# Revit family: ВПВО
name_source: partatom
category: Оборудование
units: mm (PartAtom-declared; Revit-internal decimal feet)

## family parameters
Всегда вертикально = Да
Классификация = Нет
На основе рабочей плоскости = Нет
Общий = Нет
При загрузке вырезать с полостями = Нет
Размер круглого соединителя = Использовать диаметр
Тип детали = Нормальный
Точка принадлежности помещению = Нет

## types (159) — shared parameters
00_20_Name = Осьовий вентилятор середнього тиску
Casing Material = Условный материал-отделка
Grid Material = Условный материал-отделка
Load Classification = HVAC
Maintenance zone material = <По категории>
Number of Fase = 3
Voltage = 400 В
t = 5 мм
zero-valued in all types: Отметка по умолчанию

## per-type parameters (varying)
| type | D2 | D3 | Dn | Dy | L | Lk1 | Lk2 | Lk3 | Ly | Maximum Air Flow | Power | Rk | Rk1 | t1 | Вес |
| ВПВО-400-2Д/0,55-6/25/ПАГ | 490 мм | 390 мм | 404 мм | 400 мм | 350 мм | 170 мм | 300 мм | 235 мм | 175 мм | 1450.0 л/с | 550 В·А | 200 мм | 215 мм | 345 мм | 23.4 кг |
| ВПВО-400-2Д/0,75-6/30/ПАГ | 490 мм | 390 мм | 404 мм | 400 мм | 350 мм | 170 мм | 300 мм | 235 мм | 175 мм | 1700.0 л/с | 750 В·А | 200 мм | 215 мм | 345 мм | 26.5 кг |
| ВПВО-400-2Д/1,1-6/35/ПАГ | 490 мм | 390 мм | 404 мм | 400 мм | 450 мм | 270 мм | 400 мм | 335 мм | 225 мм | 2000.0 л/с | 1100 В·А | 200 мм | 215 мм | 445 мм | 27 кг |
| ВПВО-400-2Д/1,5-6/40/ПАГ | 490 мм | 390 мм | 404 мм | 400 мм | 450 мм | 270 мм | 400 мм | 335 мм | 225 мм | 2150.0 л/с | 1500 В·А | 200 мм | 215 мм | 445 мм | 32.5 кг |
| ВПВО-400-2Д/2,2-6/45/ПАГ | 490 мм | 390 мм | 404 мм | 400 мм | 450 мм | 270 мм | 400 мм | 335 мм | 225 мм | 2350.0 л/с | 2200 В·А | 200 мм | 215 мм | 445 мм | 34.5 кг |
| ВПВО-400-2Д/2,2-8/45/ПАГ | 490 мм | 390 мм | 404 мм | 400 мм | 450 мм | 270 мм | 400 мм | 335 мм | 225 мм | 2450.0 л/с | 2200 В·А | 200 мм | 215 мм | 445 мм | 35 кг |
| ВПВО-400-4Д/0,12-6/30/ПАГ | 490 мм | 390 мм | 404 мм | 400 мм | 350 мм | 170 мм | 300 мм | 235 мм | 175 мм | 880.0 л/с | 120 В·А | 200 мм | 215 мм | 345 мм | 19.5 кг |
| ВПВО-400-4Д/0,18-6/35/ПАГ | 490 мм | 390 мм | 404 мм | 400 мм | 350 мм | 170 мм | 300 мм | 235 мм | 175 мм | 1000.0 л/с | 180 В·А | 200 мм | 215 мм | 345 мм | 19.8 кг |
| ВПВО-400-4Д/0,18-6/40/ПАГ | 490 мм | 390 мм | 404 мм | 400 мм | 350 мм | 170 мм | 300 мм | 235 мм | 175 мм | 1050.0 л/с | 180 В·А | 200 мм | 215 мм | 345 мм | 19.8 кг |
| ВПВО-400-4Д/0,25-6/45/ПАГ | 490 мм | 390 мм | 404 мм | 400 мм | 350 мм | 170 мм | 300 мм | 235 мм | 175 мм | 1180.0 л/с | 250 В·А | 200 мм | 215 мм | 345 мм | 23.2 кг |
| ВПВО-400-4Д/0,37-8/45/ПАГ | 490 мм | 390 мм | 404 мм | 400 мм | 350 мм | 170 мм | 300 мм | 235 мм | 175 мм | 1200.0 л/с | 370 В·А | 200 мм | 215 мм | 345 мм | 23.9 кг |
| ВПВО-450-2Д/0,75-6/25/ПАГ | 540 мм | 440 мм | 454 мм | 450 мм | 350 мм | 170 мм | 300 мм | 235 мм | 175 мм | 1875.0 л/с | 750 В·А | 225 мм | 240 мм | 345 мм | 36.1 кг |
| ВПВО-450-2Д/1,1-6/30/ПАГ | 540 мм | 440 мм | 454 мм | 450 мм | 450 мм | 270 мм | 400 мм | 335 мм | 225 мм | 2300.0 л/с | 1100 В·А | 225 мм | 240 мм | 445 мм | 36.6 кг |
| ВПВО-450-2Д/1,5-6/35/ПАГ | 540 мм | 440 мм | 454 мм | 450 мм | 450 мм | 270 мм | 400 мм | 335 мм | 225 мм | 2700.0 л/с | 1500 В·А | 225 мм | 240 мм | 445 мм | 42.1 кг |
| ВПВО-450-2Д/2,2-6/40/ПАГ | 540 мм | 440 мм | 454 мм | 450 мм | 450 мм | 270 мм | 400 мм | 335 мм | 225 мм | 3000.0 л/с | 2200 В·А | 225 мм | 240 мм | 445 мм | 44.1 кг |
| ВПВО-450-2Д/3-8/40/ПАГ | 540 мм | 440 мм | 454 мм | 450 мм | 450 мм | 270 мм | 400 мм | 335 мм | 225 мм | 3125.0 л/с | 3000 В·А | 225 мм | 240 мм | 445 мм | 53.6 кг |
| ВПВО-450-2Д/4-8/45/ПАГ | 540 мм | 440 мм | 454 мм | 450 мм | 550 мм | 370 мм | 500 мм | 435 мм | 275 мм | 3500.0 л/с | 4000 В·А | 225 мм | 240 мм | 545 мм | 63.7 кг |
| ВПВО-450-4Д/0,12-6/25/ПАГ | 540 мм | 440 мм | 454 мм | 450 мм | 350 мм | 170 мм | 300 мм | 235 мм | 175 мм | 950.0 л/с | 120 В·А | 225 мм | 240 мм | 345 мм | 29.1 кг |
| ВПВО-450-4Д/0,18-6/30/ПАГ | 540 мм | 440 мм | 454 мм | 450 мм | 350 мм | 170 мм | 300 мм | 235 мм | 175 мм | 1100.0 л/с | 180 В·А | 225 мм | 240 мм | 345 мм | 29.4 кг |
| ВПВО-450-4Д/0,25-6/35/ПАГ | 540 мм | 440 мм | 454 мм | 450 мм | 350 мм | 170 мм | 300 мм | 235 мм | 175 мм | 1350.0 л/с | 250 В·А | 225 мм | 240 мм | 345 мм | 32.8 кг |
| ВПВО-450-4Д/0,25-6/40/ПАГ | 540 мм | 440 мм | 454 мм | 450 мм | 350 мм | 170 мм | 300 мм | 235 мм | 175 мм | 1450.0 л/с | 250 В·А | 225 мм | 240 мм | 345 мм | 32.8 кг |
| ВПВО-450-4Д/0,37-6/45/ПАГ | 540 мм | 440 мм | 454 мм | 450 мм | 350 мм | 170 мм | 300 мм | 235 мм | 175 мм | 1600.0 л/с | 370 В·А | 225 мм | 240 мм | 345 мм | 33 кг |
| ВПВО-450-4Д/0,55-8/45/ПАГ | 540 мм | 440 мм | 454 мм | 450 мм | 350 мм | 170 мм | 300 мм | 235 мм | 175 мм | 1700.0 л/с | 550 В·А | 225 мм | 240 мм | 345 мм | 36.6 кг |
| ВПВО-500-2Д/1,1-6/25/ПАГ | 600 мм | 490 мм | 504 мм | 500 мм | 450 мм | 270 мм | 400 мм | 335 мм | 225 мм | 2350.0 л/с | 1100 В·А | 250 мм | 265 мм | 445 мм | 48.2 кг |
| ВПВО-560-2Д/1,5-6/25/ПАГ | 660 мм | 550 мм | 564 мм | 560 мм | 450 мм | 270 мм | 400 мм | 335 мм | 225 мм | 2900.0 л/с | 1500 В·А | 280 мм | 295 мм | 445 мм | 70.8 кг |
| ВПВО-630-2Д/3-8/25/ПАГ | 730 мм | 620 мм | 634 мм | 630 мм | 450 мм | 270 мм | 400 мм | 335 мм | 225 мм | 3800.0 л/с | 3000 В·А | 315 мм | 330 мм | 445 мм | 88 кг |
| ВПВО-710-2Д/7,5-6/20/ПАГ | 810 мм | 700 мм | 714 мм | 710 мм | 550 мм | 370 мм | 500 мм | 435 мм | 275 мм | 6300.0 л/с | 7500 В·А | 355 мм | 370 мм | 545 мм | 150.8 |
| ВПВО-800-4Д/1,1-6/20/ПАГ | 900 мм | 790 мм | 804 мм | 800 мм | 450 мм | 270 мм | 400 мм | 335 мм | 225 мм | 4200.0 л/с | 1100 В·А | 400 мм | 415 мм | 445 мм | 115.6 кг |
| ВПВО-900-4Д/3-8/20/ПАГ | 1015 мм | 890 мм | 904 мм | 900 мм | 550 мм | 370 мм | 500 мм | 435 мм | 275 мм | 6000.0 л/с | 3000 В·А | 450 мм | 465 мм | 545 мм | 134.8 кг |
| ВПВО-1000-4Д/5,5-8/25/ПАГ | 1115 мм | 990 мм | 1004 мм | 1000 мм | 550 мм | 370 мм | 500 мм | 435 мм | 275 мм | 8600.0 л/с | 5500 В·А | 500 мм | 515 мм | 545 мм | 200.5 кг |
| ВПВО-1120-4Д/7,5-8/25/ПАГ | 1270 мм | 1110 мм | 1124 мм | 1120 мм | 650 мм | 470 мм | 600 мм | 535 мм | 325 мм | 12200.0 л/с | 7500 В·А | 560 мм | 575 мм | 645 мм | 222 кг |
| ВПВО-1250-4Д/7,5-8/25/ПАГ | 1400 мм | 1240 мм | 1254 мм | 1250 мм | 650 мм | 470 мм | 600 мм | 535 мм | 325 мм | 12500.0 л/с | 7500 В·А | 625 мм | 640 мм | 645 мм | 241 кг |
| ВПВО-500-2Д/1,5-6/30/ПАГ | 600 мм | 490 мм | 504 мм | 500 мм | 450 мм | 270 мм | 400 мм | 335 мм | 225 мм | 2900.0 л/с | 1500 В·А | 250 мм | 265 мм | 445 мм | 53.7 кг |
| ВПВО-500-2Д/2,2-6/35/ПАГ | 600 мм | 490 мм | 504 мм | 500 мм | 450 мм | 270 мм | 400 мм | 335 мм | 225 мм | 3400.0 л/с | 2200 В·А | 250 мм | 265 мм | 445 мм | 55.7 кг |
| ВПВО-500-2Д/3-8/35/ПАГ | 600 мм | 490 мм | 504 мм | 500 мм | 450 мм | 270 мм | 400 мм | 335 мм | 225 мм | 3700.0 л/с | 3000 В·А | 250 мм | 265 мм | 445 мм | 65.3 кг |
| ВПВО-500-2Д/4-8/40/ПАГ | 600 мм | 490 мм | 504 мм | 500 мм | 550 мм | 370 мм | 500 мм | 435 мм | 275 мм | 4200.0 л/с | 4000 В·А | 250 мм | 265 мм | 545 мм | 75.4 кг |
| ВПВО-500-2Д/5,5-8/45/ПАГ | 600 мм | 490 мм | 504 мм | 500 мм | 550 мм | 370 мм | 500 мм | 435 мм | 275 мм | 4500.0 л/с | 5500 В·А | 250 мм | 265 мм | 545 мм | 96.8 кг |
| ВПВО-500-4Д/0,18-6/25/ПАГ | 600 мм | 490 мм | 504 мм | 500 мм | 350 мм | 170 мм | 300 мм | 235 мм | 175 мм | 1200.0 л/с | 180 В·А | 250 мм | 265 мм | 345 мм | 61.5 кг |
| ВПВО-500-4Д/0,25-6/30/ПАГ | 600 мм | 490 мм | 504 мм | 500 мм | 350 мм | 170 мм | 300 мм | 235 мм | 175 мм | 1460.0 л/с | 250 В·А | 250 мм | 265 мм | 345 мм | 61.7 кг |
| ВПВО-500-4Д/0,37-6/35/ПАГ | 600 мм | 490 мм | 504 мм | 500 мм | 350 мм | 170 мм | 300 мм | 235 мм | 175 мм | 1700.0 л/с | 370 В·А | 250 мм | 265 мм | 345 мм | 64.8 кг |
| ВПВО-500-4Д/0,37-6/40/ПАГ | 600 мм | 490 мм | 504 мм | 500 мм | 350 мм | 170 мм | 300 мм | 235 мм | 175 мм | 1800.0 л/с | 370 В·А | 250 мм | 265 мм | 345 мм | 64.8 кг |
| ВПВО-500-4Д/0,55-6/45/ПАГ | 600 мм | 490 мм | 504 мм | 500 мм | 450 мм | 270 мм | 400 мм | 335 мм | 225 мм | 2100.0 л/с | 550 В·А | 250 мм | 265 мм | 445 мм | 65.6 кг |
| ВПВО-500-4Д/0,75-8/45/ПАГ | 600 мм | 490 мм | 504 мм | 500 мм | 450 мм | 270 мм | 400 мм | 335 мм | 225 мм | 2300.0 л/с | 750 В·А | 250 мм | 265 мм | 445 мм | 71.4 кг |
| ВПВО-560-2Д/2,2/6/30/ПАГ | 660 мм | 550 мм | 564 мм | 560 мм | 450 мм | 270 мм | 400 мм | 335 мм | 225 мм | 3500.0 л/с | 2200 В·А | 280 мм | 295 мм | 445 мм | 72.8 кг |
| ВПВО-560-2Д/3-8/30/ПАГ | 660 мм | 550 мм | 564 мм | 560 мм | 450 мм | 270 мм | 400 мм | 335 мм | 225 мм | 3900.0 л/с | 3000 В·А | 280 мм | 295 мм | 445 мм | 82.4 кг |
| ВПВО-560-2Д/4-8/35/ПАГ | 660 мм | 550 мм | 564 мм | 560 мм | 550 мм | 370 мм | 500 мм | 435 мм | 275 мм | 4800.0 л/с | 4000 В·А | 280 мм | 295 мм | 545 мм | 92.5 кг |
| ВПВО-560-2Д/5,5-8/40/ПАГ | 660 мм | 550 мм | 564 мм | 560 мм | 550 мм | 370 мм | 500 мм | 435 мм | 275 мм | 5150.0 л/с | 5500 В·А | 280 мм | 295 мм | 545 мм | 113.9 кг |
| ВПВО-560-2Д/7,5-8/45/ПАГ | 660 мм | 550 мм | 564 мм | 560 мм | 550 мм | 370 мм | 500 мм | 435 мм | 275 мм | 6000.0 л/с | 7500 В·А | 280 мм | 295 мм | 545 мм | 117.9 кг |
| ВПВО-560-4Д/0,25-6/25/ПАГ | 660 мм | 550 мм | 564 мм | 560 мм | 350 мм | 170 мм | 300 мм | 235 мм | 175 мм | 1400.0 л/с | 250 В·А | 280 мм | 295 мм | 345 мм | 61.5 кг |
| ВПВО-560-4Д/0,37-6/30/ПАГ | 660 мм | 550 мм | 564 мм | 560 мм | 350 мм | 170 мм | 300 мм | 235 мм | 175 мм | 1800.0 л/с | 370 В·А | 280 мм | 295 мм | 345 мм | 61.7 кг |
| ВПВО-560-4Д/0,55-6/35/ПАГ | 660 мм | 550 мм | 564 мм | 560 мм | 350 мм | 170 мм | 300 мм | 235 мм | 175 мм | 2150.0 л/с | 550 В·А | 280 мм | 295 мм | 345 мм | 64.8 кг |
| ВПВО-560-4Д/0,55-6/40/ПАГ | 660 мм | 550 мм | 564 мм | 560 мм | 350 мм | 170 мм | 300 мм | 235 мм | 175 мм | 2400.0 л/с | 550 В·А | 280 мм | 295 мм | 345 мм | 64.8 кг |
| ВПВО-560-4Д/0,75-6/45/ПАГ | 660 мм | 550 мм | 564 мм | 560 мм | 450 мм | 270 мм | 400 мм | 335 мм | 225 мм | 2600.0 л/с | 750 В·А | 280 мм | 295 мм | 445 мм | 65.6 кг |
| ВПВО-560-4Д/1,1-8/45/ПАГ | 660 мм | 550 мм | 564 мм | 560 мм | 450 мм | 270 мм | 400 мм | 335 мм | 225 мм | 3000.0 л/с | 1100 В·А | 280 мм | 295 мм | 445 мм | 71.4 кг |
| ВПВО-630-2Д/4-8/30/ПАГ | 730 мм | 620 мм | 634 мм | 630 мм | 550 мм | 370 мм | 500 мм | 435 мм | 275 мм | 4700.0 л/с | 4000 В·А | 315 мм | 330 мм | 545 мм | 98.1 кг |
| ВПВО-630-2Д/5,5-8/35/ПАГ | 730 мм | 620 мм | 634 мм | 630 мм | 550 мм | 370 мм | 500 мм | 435 мм | 275 мм | 6000.0 л/с | 5500 В·А | 315 мм | 330 мм | 545 мм | 119.5 кг |
| ВПВО-630-2Д/7,5-8/40/ПАГ | 730 мм | 620 мм | 634 мм | 630 мм | 550 мм | 370 мм | 500 мм | 435 мм | 275 мм | 6800.0 л/с | 7500 В·А | 315 мм | 330 мм | 545 мм | 123.5 кг |
| ВПВО-630-2Д/9,2-6/30/ПАГ | 730 мм | 620 мм | 634 мм | 630 мм | 650 мм | 470 мм | 600 мм | 535 мм | 325 мм | 7200.0 л/с | 9200 В·А | 315 мм | 330 мм | 645 мм | 130.1 кг |
| ВПВО-630-2Д/11-6/32,5/ПАГ | 730 мм | 620 мм | 634 мм | 630 мм | 650 мм | 470 мм | 600 мм | 535 мм | 325 мм | 7500.0 л/с | 11000 В·А | 315 мм | 330 мм | 645 мм | 154.1 кг |
| ВПВО-630-2Д/11-6/35/ПАГ | 730 мм | 620 мм | 634 мм | 630 мм | 650 мм | 470 мм | 600 мм | 535 мм | 325 мм | 8300.0 л/с | 11000 В·А | 315 мм | 330 мм | 645 мм | 154.1 кг |
| ВПВО-630-2Д/15-6/37,5/ПАГ | 730 мм | 620 мм | 634 мм | 630 мм | 750 мм | 570 мм | 700 мм | 635 мм | 375 мм | 8400.0 л/с | 15000 В·А | 315 мм | 330 мм | 745 мм | 166.7 кг |
| ВПВО-630-2Д/15-6/40/ПАГ | 730 мм | 620 мм | 634 мм | 630 мм | 750 мм | 570 мм | 700 мм | 635 мм | 375 мм | 8650.0 л/с | 15000 В·А | 315 мм | 330 мм | 745 мм | 166.7 кг |
| ВПВО-630-2Д/18,5-6/45/ПАГ | 730 мм | 620 мм | 634 мм | 630 мм | 750 мм | 570 мм | 700 мм | 635 мм | 375 мм | 9400.0 л/с | 18500 В·А | 315 мм | 330 мм | 745 мм | 179.8 кг |
| ВПВО-630-4Д/0,37-8/25/ПАГ | 730 мм | 620 мм | 634 мм | 630 мм | 350 мм | 170 мм | 300 мм | 235 мм | 175 мм | 1900.0 л/с | 370 В·А | 315 мм | 330 мм | 345 мм | 67.9 кг |
| ВПВО-630-4Д/0,55-8/30/ПАГ | 730 мм | 620 мм | 634 мм | 630 мм | 350 мм | 170 мм | 300 мм | 235 мм | 175 мм | 2500.0 л/с | 550 В·А | 315 мм | 330 мм | 345 мм | 71 кг |
| ВПВО-630-4Д/0,75-8/35/ПАГ | 730 мм | 620 мм | 634 мм | 630 мм | 450 мм | 270 мм | 400 мм | 335 мм | 225 мм | 2900.0 л/с | 750 В·А | 315 мм | 330 мм | 445 мм | 71.8 кг |
| ВПВО-630-4Д/1,1-8/40/ПАГ | 730 мм | 620 мм | 634 мм | 630 мм | 450 мм | 270 мм | 400 мм | 335 мм | 225 мм | 3400.0 л/с | 1100 В·А | 315 мм | 330 мм | 445 мм | 77 кг |
| ВПВО-630-4Д/1,5-6/32,5/ПАГ | 730 мм | 620 мм | 634 мм | 630 мм | 450 мм | 270 мм | 400 мм | 335 мм | 225 мм | 3900.0 л/с | 1500 В·А | 315 мм | 330 мм | 445 мм | 81.1 кг |
| ВПВО-630-4Д/1,5-8/45/ПАГ | 730 мм | 620 мм | 634 мм | 630 мм | 450 мм | 270 мм | 400 мм | 335 мм | 225 мм | 4000.0 л/с | 1500 В·А | 315 мм | 330 мм | 445 мм | 80 кг |
| ВПВО-630-4Д/1,5-6/37,5/ПАГ | 730 мм | 620 мм | 634 мм | 630 мм | 450 мм | 270 мм | 400 мм | 335 мм | 225 мм | 4150.0 л/с | 1500 В·А | 315 мм | 330 мм | 445 мм | 81.1 кг |
| ВПВО-630-4Д/2,2-6/40/ПАГ | 730 мм | 620 мм | 634 мм | 630 мм | 450 мм | 270 мм | 400 мм | 335 мм | 225 мм | 4300.0 л/с | 2200 В·А | 315 мм | 330 мм | 445 мм | 83.2 кг |
| ВПВО-630-4Д/2,2-6/45/ПАГ | 730 мм | 620 мм | 634 мм | 630 мм | 450 мм | 270 мм | 400 мм | 335 мм | 225 мм | 4700.0 л/с | 2200 В·А | 315 мм | 330 мм | 445 мм | 83.2 кг |
| ВПВО-710-2Д/9,2-6/25/ПАГ | 810 мм | 700 мм | 714 мм | 710 мм | 650 мм | 470 мм | 600 мм | 535 мм | 325 мм | 7900.0 л/с | 9200 В·А | 355 мм | 370 мм | 645 мм | 156.3 |
| ВПВО-710-2Д/15-6/30/ПАГ | 810 мм | 700 мм | 714 мм | 710 мм | 750 мм | 570 мм | 700 мм | 635 мм | 375 мм | 9400.0 л/с | 15000 В·А | 355 мм | 370 мм | 745 мм | 192.9 |
| ВПВО-710-2Д/15-6/32,5/ПАГ | 810 мм | 700 мм | 714 мм | 710 мм | 750 мм | 570 мм | 700 мм | 635 мм | 375 мм | 10400.0 л/с | 15000 В·А | 355 мм | 370 мм | 745 мм | 192.9 |
| ВПВО-710-2Д/18,5-6/35/ПАГ | 810 мм | 700 мм | 714 мм | 710 мм | 750 мм | 570 мм | 700 мм | 635 мм | 375 мм | 10800.0 л/с | 18500 В·А | 355 мм | 370 мм | 745 мм | 206 |
| ВПВО-710-2Д/18,5-6/37,5/ПАГ | 810 мм | 700 мм | 714 мм | 710 мм | 750 мм | 570 мм | 700 мм | 635 мм | 375 мм | 11400.0 л/с | 18500 В·А | 355 мм | 370 мм | 745 мм | 206 |
| ВПВО-710-2Д/22-6/40/ПАГ | 810 мм | 700 мм | 714 мм | 710 мм | 850 мм | 670 мм | 800 мм | 735 мм | 425 мм | 12000.0 л/с | 22000 В·А | 355 мм | 370 мм | 845 мм | 246 |
| ВПВО-710-4Д/0,75-6/20/ПАГ | 810 мм | 700 мм | 714 мм | 710 мм | 450 мм | 270 мм | 400 мм | 335 мм | 225 мм | 3200.0 л/с | 750 В·А | 355 мм | 370 мм | 445 мм | 99.1 |
| ВПВО-710-4Д/1,1-6/25/ПАГ | 810 мм | 700 мм | 714 мм | 710 мм | 450 мм | 270 мм | 400 мм | 335 мм | 225 мм | 4000.0 л/с | 1100 В·А | 355 мм | 370 мм | 445 мм | 104.3 |
| ВПВО-710-4Д/1,5-6/30/ПАГ | 810 мм | 700 мм | 714 мм | 710 мм | 450 мм | 270 мм | 400 мм | 335 мм | 225 мм | 4700.0 л/с | 1500 В·А | 355 мм | 370 мм | 445 мм | 107.3 |
| ВПВО-710-4Д/2,2-6/32,5/ПАГ | 810 мм | 700 мм | 714 мм | 710 мм | 450 мм | 270 мм | 400 мм | 335 мм | 225 мм | 5300.0 л/с | 2200 В·А | 355 мм | 370 мм | 445 мм | 109.4 |
| ВПВО-710-4Д/2,2-6/35/ПАГ | 810 мм | 700 мм | 714 мм | 710 мм | 450 мм | 270 мм | 400 мм | 335 мм | 225 мм | 5500.0 л/с | 2200 В·А | 355 мм | 370 мм | 445 мм | 109.4 |
| ВПВО-710-4Д/2,2-6/37,5/ПАГ | 810 мм | 700 мм | 714 мм | 710 мм | 450 мм | 270 мм | 400 мм | 335 мм | 225 мм | 5700.0 л/с | 2200 В·А | 355 мм | 370 мм | 445 мм | 109.4 |
| ВПВО-710-4Д/3-6/40/ПАГ | 810 мм | 700 мм | 714 мм | 710 мм | 550 мм | 370 мм | 500 мм | 435 мм | 275 мм | 5900.0 л/с | 3000 В·А | 355 мм | 370 мм | 545 мм | 118.3 |
| ВПВО-710-4Д/4-6/45/ПАГ | 810 мм | 700 мм | 714 мм | 710 мм | 550 мм | 370 мм | 500 мм | 435 мм | 275 мм | 5900.0 л/с | 6400 В·А | 355 мм | 370 мм | 545 мм | 129.4 |
| ВПВО-800-4Д/1,5-6/25/ПАГ | 900 мм | 790 мм | 804 мм | 800 мм | 450 мм | 270 мм | 400 мм | 335 мм | 225 мм | 5100.0 л/с | 1500 В·А | 400 мм | 415 мм | 445 мм | 118.6 кг |
| ВПВО-800-4Д/2,2-6/30/ПАГ | 900 мм | 790 мм | 804 мм | 800 мм | 450 мм | 270 мм | 400 мм | 335 мм | 225 мм | 5850.0 л/с | 2200 В·А | 400 мм | 415 мм | 445 мм | 120.7 кг |
| ВПВО-800-4Д/3-6/32,5/ПАГ | 900 мм | 790 мм | 804 мм | 800 мм | 550 мм | 370 мм | 500 мм | 435 мм | 275 мм | 6800.0 л/с | 3000 В·А | 400 мм | 415 мм | 545 мм | 129.6 кг |
| ВПВО-800-4Д/3-6/35/ПАГ | 900 мм | 790 мм | 804 мм | 800 мм | 550 мм | 370 мм | 500 мм | 435 мм | 275 мм | 7400.0 л/с | 3000 В·А | 400 мм | 415 мм | 545 мм | 129.6 кг |
| ВПВО-800-4Д/4-6/37,5/ПАГ | 900 мм | 790 мм | 804 мм | 800 мм | 550 мм | 370 мм | 500 мм | 435 мм | 275 мм | 7500.0 л/с | 4000 В·А | 400 мм | 415 мм | 545 мм | 140.7 кг |
| ВПВО-800-4Д/4-6/40/ПАГ | 900 мм | 790 мм | 804 мм | 800 мм | 550 мм | 370 мм | 500 мм | 435 мм | 275 мм | 8050.0 л/с | 4000 В·А | 400 мм | 415 мм | 545 мм | 140.7 кг |
| ВПВО-800-4Д/5,5-6/45/ПАГ | 900 мм | 790 мм | 804 мм | 800 мм | 550 мм | 370 мм | 500 мм | 435 мм | 275 мм | 8700.0 л/с | 5500 В·А | 400 мм | 415 мм | 545 мм | 157.6 кг |
| ВПВО-800-6Д/0,37-6/20/ПАГ | 900 мм | 790 мм | 804 мм | 800 мм | 450 мм | 270 мм | 400 мм | 335 мм | 225 мм | 2700.0 л/с | 370 В·А | 400 мм | 415 мм | 445 мм | 109.6 кг |
| ВПВО-800-6Д/0,55-6/25/ПАГ | 900 мм | 790 мм | 804 мм | 800 мм | 450 мм | 270 мм | 400 мм | 335 мм | 225 мм | 3600.0 л/с | 550 В·А | 400 мм | 415 мм | 445 мм | 111.1 кг |
| ВПВО-800-6Д/0,75-6/30/ПАГ | 900 мм | 790 мм | 804 мм | 800 мм | 450 мм | 270 мм | 400 мм | 335 мм | 225 мм | 4200.0 л/с | 750 В·А | 400 мм | 415 мм | 445 мм | 116.4 кг |
| ВПВО-800-6Д/0,75-6/32,5/ПАГ | 900 мм | 790 мм | 804 мм | 800 мм | 450 мм | 270 мм | 400 мм | 335 мм | 225 мм | 4400.0 л/с | 750 В·А | 400 мм | 415 мм | 445 мм | 116.4 кг |
| ВПВО-800-6Д/1,1-6/35/ПАГ | 900 мм | 790 мм | 804 мм | 800 мм | 450 мм | 270 мм | 400 мм | 335 мм | 225 мм | 5000.0 л/с | 1100 В·А | 400 мм | 415 мм | 445 мм | 116.5 кг |
| ВПВО-800-6Д/1,1-6/37,5/ПАГ | 900 мм | 790 мм | 804 мм | 800 мм | 450 мм | 270 мм | 400 мм | 335 мм | 225 мм | 5200.0 л/с | 1100 В·А | 400 мм | 415 мм | 445 мм | 116.5 кг |
| ВПВО-800-6Д/1,1-6/40/ПАГ | 900 мм | 790 мм | 804 мм | 800 мм | 450 мм | 270 мм | 400 мм | 335 мм | 225 мм | 5400.0 л/с | 1100 В·А | 400 мм | 415 мм | 445 мм | 116.5 кг |
| ВПВО-800-6Д/1,5-6/45/ПАГ | 900 мм | 790 мм | 804 мм | 800 мм | 550 мм | 370 мм | 500 мм | 435 мм | 275 мм | 5700.0 л/с | 1500 В·А | 400 мм | 415 мм | 545 мм | 124.6 кг |
| ВПВО-900-4Д/4-8/25/ПАГ | 1015 мм | 890 мм | 904 мм | 900 мм | 550 мм | 370 мм | 500 мм | 435 мм | 275 мм | 7300.0 л/с | 4000 В·А | 450 мм | 465 мм | 545 мм | 145.9 кг |
| ВПВО-900-4Д/5,5-8/30/ПАГ | 1015 мм | 890 мм | 904 мм | 900 мм | 550 мм | 370 мм | 500 мм | 435 мм | 275 мм | 8800.0 л/с | 5500 В·А | 450 мм | 465 мм | 545 мм | 162.8 кг |
| ВПВО-900-4Д/5,5-8/32,5/ПАГ | 1015 мм | 890 мм | 904 мм | 900 мм | 550 мм | 370 мм | 500 мм | 435 мм | 275 мм | 9000.0 л/с | 5500 В·А | 450 мм | 465 мм | 545 мм | 162.8 кг |
| ВПВО-900-4Д/7,5-8/35/ПАГ | 1015 мм | 890 мм | 904 мм | 900 мм | 650 мм | 470 мм | 600 мм | 535 мм | 325 мм | 9700.0 л/с | 7500 В·А | 450 мм | 465 мм | 645 мм | 165.3 кг |
| ВПВО-900-4Д/7,5-8/37,5/ПАГ | 1015 мм | 890 мм | 904 мм | 900 мм | 650 мм | 470 мм | 600 мм | 535 мм | 325 мм | 10400.0 л/с | 7500 В·А | 450 мм | 465 мм | 645 мм | 165.3 кг |
| ВПВО-900-4Д/7,5-8/40/ПАГ | 1015 мм | 890 мм | 904 мм | 900 мм | 650 мм | 470 мм | 600 мм | 535 мм | 325 мм | 10700.0 л/с | 7500 В·А | 450 мм | 465 мм | 645 мм | 165.3 кг |
| ВПВО-900-4Д/11-8/45/ПАГ | 1015 мм | 890 мм | 904 мм | 900 мм | 750 мм | 570 мм | 700 мм | 635 мм | 375 мм | 12000.0 л/с | 11000 В·А | 450 мм | 465 мм | 745 мм | 199.6 кг |
| ВПВО-900-6Д/0,75-8/20/ПАГ | 1015 мм | 890 мм | 904 мм | 900 мм | 450 мм | 270 мм | 400 мм | 335 мм | 225 мм | 3900.0 л/с | 750 В·А | 450 мм | 465 мм | 445 мм | 121.6 кг |
| ВПВО-900-6Д/1,1-8/25/ПАГ | 1015 мм | 890 мм | 904 мм | 900 мм | 450 мм | 270 мм | 400 мм | 335 мм | 225 мм | 4700.0 л/с | 1100 В·А | 450 мм | 465 мм | 445 мм | 121.7 кг |
| ВПВО-900-6Д/1,5-8/30/ПАГ | 1015 мм | 890 мм | 904 мм | 900 мм | 550 мм | 370 мм | 500 мм | 435 мм | 275 мм | 5700.0 л/с | 1500 В·А | 450 мм | 465 мм | 545 мм | 129.8 кг |
| ВПВО-900-6Д/1,5-8/32,5/ПАГ | 1015 мм | 890 мм | 904 мм | 900 мм | 550 мм | 370 мм | 500 мм | 435 мм | 275 мм | 5900.0 л/с | 1500 В·А | 450 мм | 465 мм | 545 мм | 129.8 кг |
| ВПВО-900-6Д/2,2-8/35/ПАГ | 1015 мм | 890 мм | 904 мм | 900 мм | 550 мм | 370 мм | 500 мм | 435 мм | 275 мм | 6700.0 л/с | 2200 В·А | 450 мм | 465 мм | 545 мм | 135.3 кг |
| ВПВО-900-6Д/2,2-8/37,5/ПАГ | 1015 мм | 890 мм | 904 мм | 900 мм | 550 мм | 370 мм | 500 мм | 435 мм | 275 мм | 7000.0 л/с | 2200 В·А | 450 мм | 465 мм | 545 мм | 135.3 кг |
| ВПВО-900-6Д/2,2-8/40/ПАГ | 1015 мм | 890 мм | 904 мм | 900 мм | 550 мм | 370 мм | 500 мм | 435 мм | 275 мм | 7100.0 л/с | 2200 В·А | 450 мм | 465 мм | 545 мм | 135.3 кг |
| ВПВО-900-6Д/3-8/45/ПАГ | 1015 мм | 890 мм | 904 мм | 900 мм | 650 мм | 470 мм | 600 мм | 535 мм | 325 мм | 8050.0 л/с | 3000 В·А | 450 мм | 465 мм | 645 мм | 155.8 кг |
| ВПВО-1000-4Д/7,5-8/30/ПАГ | 1115 мм | 990 мм | 1004 мм | 1000 мм | 650 мм | 470 мм | 600 мм | 535 мм | 325 мм | 10700.0 л/с | 7500 В·А | 500 мм | 515 мм | 645 мм | 203 кг |
| ВПВО-1000-4Д/7,5-8/32,5/ПАГ | 1115 мм | 990 мм | 1004 мм | 1000 мм | 650 мм | 470 мм | 600 мм | 535 мм | 325 мм | 12000.0 л/с | 7500 В·А | 500 мм | 515 мм | 645 мм | 203 кг |
| ВПВО-1000-4Д/9,2-8/35/ПАГ | 1115 мм | 990 мм | 1004 мм | 1000 мм | 650 мм | 470 мм | 600 мм | 535 мм | 325 мм | 12800.0 л/с | 9200 В·А | 500 мм | 515 мм | 645 мм | 233.5 кг |
| ВПВО-1000-4Д/11-8/37,5/ПАГ | 1115 мм | 990 мм | 1004 мм | 1000 мм | 800 мм | 620 мм | 750 мм | 685 мм | 400 мм | 13900.0 л/с | 11000 В·А | 500 мм | 515 мм | 795 мм | 237.3 кг |
| ВПВО-1000-4Д/11-8/40/ПАГ | 1115 мм | 990 мм | 1004 мм | 1000 мм | 800 мм | 620 мм | 750 мм | 685 мм | 400 мм | 14500.0 л/с | 11000 В·А | 500 мм | 515 мм | 795 мм | 237.3 кг |
| ВПВО-1000-4Д/15-8/45/ПАГ | 1115 мм | 990 мм | 1004 мм | 1000 мм | 800 мм | 620 мм | 750 мм | 685 мм | 400 мм | 15800.0 л/с | 15000 В·А | 500 мм | 515 мм | 795 мм | 256.4 кг |
| ВПВО-1000-4Д/18,5-8/50/ПАГ | 1115 мм | 990 мм | 1004 мм | 1000 мм | 900 мм | 720 мм | 850 мм | 785 мм | 450 мм | 17200.0 л/с | 18500 В·А | 500 мм | 515 мм | 895 мм | 301.9 кг |
| ВПВО-1000-6Д/1,5-8/25/ПАГ | 1115 мм | 990 мм | 1004 мм | 1000 мм | 550 мм | 370 мм | 500 мм | 435 мм | 275 мм | 5800.0 л/с | 1500 В·А | 500 мм | 515 мм | 545 мм | 167.5 кг |
| ВПВО-1000-6Д/2,2-8/30/ПАГ | 1115 мм | 990 мм | 1004 мм | 1000 мм | 550 мм | 370 мм | 500 мм | 435 мм | 275 мм | 7200.0 л/с | 2200 В·А | 500 мм | 515 мм | 545 мм | 173 кг |
| ВПВО-1000-6Д/2,2-8/32,5/ПАГ | 1115 мм | 990 мм | 1004 мм | 1000 мм | 550 мм | 370 мм | 500 мм | 435 мм | 275 мм | 7700.0 л/с | 2200 В·А | 500 мм | 515 мм | 545 мм | 173 кг |
| ВПВО-1000-6Д/3-8/35/ПАГ | 1115 мм | 990 мм | 1004 мм | 1000 мм | 650 мм | 470 мм | 600 мм | 535 мм | 325 мм | 8650.0 л/с | 3000 В·А | 500 мм | 515 мм | 645 мм | 193.5 кг |
| ВПВО-1000-6Д/3-8/37,5/ПАГ | 1115 мм | 990 мм | 1004 мм | 1000 мм | 650 мм | 470 мм | 600 мм | 535 мм | 325 мм | 9000.0 л/с | 3000 В·А | 500 мм | 515 мм | 645 мм | 193.5 кг |
| ВПВО-1000-6Д/4-8/40/ПАГ | 1115 мм | 990 мм | 1004 мм | 1000 мм | 650 мм | 470 мм | 600 мм | 535 мм | 325 мм | 9700.0 л/с | 4000 В·А | 500 мм | 515 мм | 645 мм | 203.5 кг |
| ВПВО-1000-6Д/5,5-8/45/ПАГ | 1115 мм | 990 мм | 1004 мм | 1000 мм | 650 мм | 470 мм | 600 мм | 535 мм | 325 мм | 10400.0 л/с | 5500 В·А | 500 мм | 515 мм | 645 мм | 207.5 кг |
| ВПВО-1000-6Д/5,5-8/50/ПАГ | 1115 мм | 990 мм | 1004 мм | 1000 мм | 650 мм | 470 мм | 600 мм | 535 мм | 325 мм | 11600.0 л/с | 5500 В·А | 500 мм | 515 мм | 645 мм | 207.5 кг |
| ВПВО-1120-4Д/11-8/30/ПАГ | 1270 мм | 1110 мм | 1124 мм | 1120 мм | 800 мм | 620 мм | 750 мм | 685 мм | 400 мм | 15200.0 л/с | 11000 В·А | 560 мм | 575 мм | 795 мм | 256.3 кг |
| ВПВО-1120-4Д/11-8/32,5/ПАГ | 1270 мм | 1110 мм | 1124 мм | 1120 мм | 800 мм | 620 мм | 750 мм | 685 мм | 400 мм | 16500.0 л/с | 11000 В·А | 560 мм | 575 мм | 795 мм | 256.3 кг |
| ВПВО-1120-4Д/15-8/35/ПАГ | 1270 мм | 1110 мм | 1124 мм | 1120 мм | 800 мм | 620 мм | 750 мм | 685 мм | 400 мм | 18000.0 л/с | 15000 В·А | 560 мм | 575 мм | 795 мм | 275.4 кг |
| ВПВО-1120-4Д/18,5-8/37,5/ПАГ | 1270 мм | 1110 мм | 1124 мм | 1120 мм | 900 мм | 720 мм | 850 мм | 785 мм | 450 мм | 19200.0 л/с | 18500 В·А | 560 мм | 575 мм | 895 мм | 320.9 кг |
| ВПВО-1120-4Д/18,5-8/40/ПАГ | 1270 мм | 1110 мм | 1124 мм | 1120 мм | 900 мм | 720 мм | 850 мм | 785 мм | 450 мм | 20500.0 л/с | 18500 В·А | 560 мм | 575 мм | 895 мм | 320.9 кг |
| ВПВО-1120-4Д/22-8/45/ПАГ | 1270 мм | 1110 мм | 1124 мм | 1120 мм | 900 мм | 720 мм | 850 мм | 785 мм | 450 мм | 22200.0 л/с | 22000 В·А | 560 мм | 575 мм | 895 мм | 334.2 кг |
| ВПВО-1120-6Д/2,2-8/25/ПАГ | 1270 мм | 1110 мм | 1124 мм | 1120 мм | 550 мм | 370 мм | 500 мм | 435 мм | 275 мм | 8300.0 л/с | 2200 В·А | 560 мм | 575 мм | 545 мм | 192 кг |
| ВПВО-1120-6Д/3-8/30/ПАГ | 1270 мм | 1110 мм | 1124 мм | 1120 мм | 650 мм | 470 мм | 600 мм | 535 мм | 325 мм | 10000.0 л/с | 3000 В·А | 560 мм | 575 мм | 645 мм | 212.5 кг |
| ВПВО-1120-6Д/4-8/32,5/ПАГ | 1270 мм | 1110 мм | 1124 мм | 1120 мм | 650 мм | 470 мм | 600 мм | 535 мм | 325 мм | 11400.0 л/с | 4000 В·А | 560 мм | 575 мм | 645 мм | 222.5 кг |
| ВПВО-1120-6Д/4-8/35/ПАГ | 1270 мм | 1110 мм | 1124 мм | 1120 мм | 650 мм | 470 мм | 600 мм | 535 мм | 325 мм | 12000.0 л/с | 4000 В·А | 560 мм | 575 мм | 645 мм | 222.5 кг |
| ВПВО-1120-6Д/5,5-8/37,5/ПАГ | 1270 мм | 1110 мм | 1124 мм | 1120 мм | 650 мм | 470 мм | 600 мм | 535 мм | 325 мм | 12800.0 л/с | 5500 В·А | 560 мм | 575 мм | 645 мм | 226.5 кг |
| ВПВО-1120-6Д/5,5-8/40/ПАГ | 1270 мм | 1110 мм | 1124 мм | 1120 мм | 650 мм | 470 мм | 600 мм | 535 мм | 325 мм | 13900.0 л/с | 5500 В·А | 560 мм | 575 мм | 645 мм | 226.5 кг |
| ВПВО-1120-6Д/7,5-8/45/ПАГ | 1270 мм | 1110 мм | 1124 мм | 1120 мм | 800 мм | 620 мм | 750 мм | 685 мм | 400 мм | 14700.0 л/с | 7500 В·А | 560 мм | 575 мм | 795 мм | 254.8 кг |
| ВПВО-1120-6Д/9,2-8/50/ПАГ | 1270 мм | 1110 мм | 1124 мм | 1120 мм | 800 мм | 620 мм | 750 мм | 685 мм | 400 мм | 16400.0 л/с | 9200 В·А | 560 мм | 575 мм | 795 мм | 272.5 кг |
| ВПВО-1250-4Д/11-8/30/ПАГ | 1400 мм | 1240 мм | 1254 мм | 1250 мм | 800 мм | 620 мм | 750 мм | 685 мм | 400 мм | 17700.0 л/с | 11000 В·А | 625 мм | 640 мм | 795 мм | 275.3 кг |
| ВПВО-1250-4Д/15-8/32,5/ПАГ | 1400 мм | 1240 мм | 1254 мм | 1250 мм | 800 мм | 620 мм | 750 мм | 685 мм | 400 мм | 19400.0 л/с | 15000 В·А | 625 мм | 640 мм | 795 мм | 294.4 кг |
| ВПВО-1250-4Д/15-8/35/ПАГ | 1400 мм | 1240 мм | 1254 мм | 1250 мм | 800 мм | 620 мм | 750 мм | 685 мм | 400 мм | 21100.0 л/с | 15000 В·А | 625 мм | 640 мм | 795 мм | 294.4 кг |
| ВПВО-1250-4Д/18,5-8/37,5/ПАГ | 1400 мм | 1240 мм | 1254 мм | 1250 мм | 900 мм | 720 мм | 850 мм | 785 мм | 450 мм | 23300.0 л/с | 18500 В·А | 625 мм | 640 мм | 895 мм | 339.9 кг |
| ВПВО-1250-4Д/22-8/40/ПАГ | 1400 мм | 1240 мм | 1254 мм | 1250 мм | 900 мм | 720 мм | 850 мм | 785 мм | 450 мм | 25000.0 л/с | 22000 В·А | 625 мм | 640 мм | 895 мм | 353.2 кг |
| ВПВО-1250-4Д/30-8/45/ПАГ | 1400 мм | 1240 мм | 1254 мм | 1250 мм | 900 мм | 720 мм | 850 мм | 785 мм | 450 мм | 27800.0 л/с | 30000 В·А | 625 мм | 640 мм | 895 мм | 416.2 кг |
| ВПВО-1250-6Д/2,2-8/25/ПАГ | 1400 мм | 1240 мм | 1254 мм | 1250 мм | 550 мм | 370 мм | 500 мм | 435 мм | 275 мм | 8750.0 л/с | 2200 В·А | 625 мм | 640 мм | 545 мм | 211 кг |
| ВПВО-1250-6Д/3-8/30/ПАГ | 1400 мм | 1240 мм | 1254 мм | 1250 мм | 650 мм | 470 мм | 600 мм | 535 мм | 325 мм | 11500.0 л/с | 3000 В·А | 625 мм | 640 мм | 645 мм | 231.5 кг |
| ВПВО-1250-6Д/4-8/32,5/ПАГ | 1400 мм | 1240 мм | 1254 мм | 1250 мм | 650 мм | 470 мм | 600 мм | 535 мм | 325 мм | 12800.0 л/с | 4000 В·А | 625 мм | 640 мм | 645 мм | 241.5 кг |
| ВПВО-1250-6Д/5,5-8/35/ПАГ | 1400 мм | 1240 мм | 1254 мм | 1250 мм | 650 мм | 470 мм | 600 мм | 535 мм | 325 мм | 14000.0 л/с | 5500 В·А | 625 мм | 640 мм | 645 мм | 245.5 кг |
| ВПВО-1250-6Д/5,5-8/37,5/ПАГ | 1400 мм | 1240 мм | 1254 мм | 1250 мм | 650 мм | 470 мм | 600 мм | 535 мм | 325 мм | 15600.0 л/с | 5500 В·А | 625 мм | 640 мм | 645 мм | 245.5 кг |
| ВПВО-1250-6Д/7,5-8/40/ПАГ | 1400 мм | 1240 мм | 1254 мм | 1250 мм | 800 мм | 620 мм | 750 мм | 685 мм | 400 мм | 16000.0 л/с | 7500 В·А | 625 мм | 640 мм | 795 мм | 273.8 кг |
| ВПВО-1250-6Д/9,2-8/45/ПАГ | 1400 мм | 1240 мм | 1254 мм | 1250 мм | 800 мм | 620 мм | 750 мм | 685 мм | 400 мм | 18600.0 л/с | 9200 В·А | 625 мм | 640 мм | 795 мм | 291.5 кг |
| ВПВО-1250-6Д/11-8/50/ПАГ | 1400 мм | 1240 мм | 1254 мм | 1250 мм | 800 мм | 620 мм | 750 мм | 685 мм | 400 мм | 19150.0 л/с | 11000 В·А | 625 мм | 640 мм | 795 мм | 299.3 кг |

note: column(s) folded — value = type name in every type: 00_20_Type
